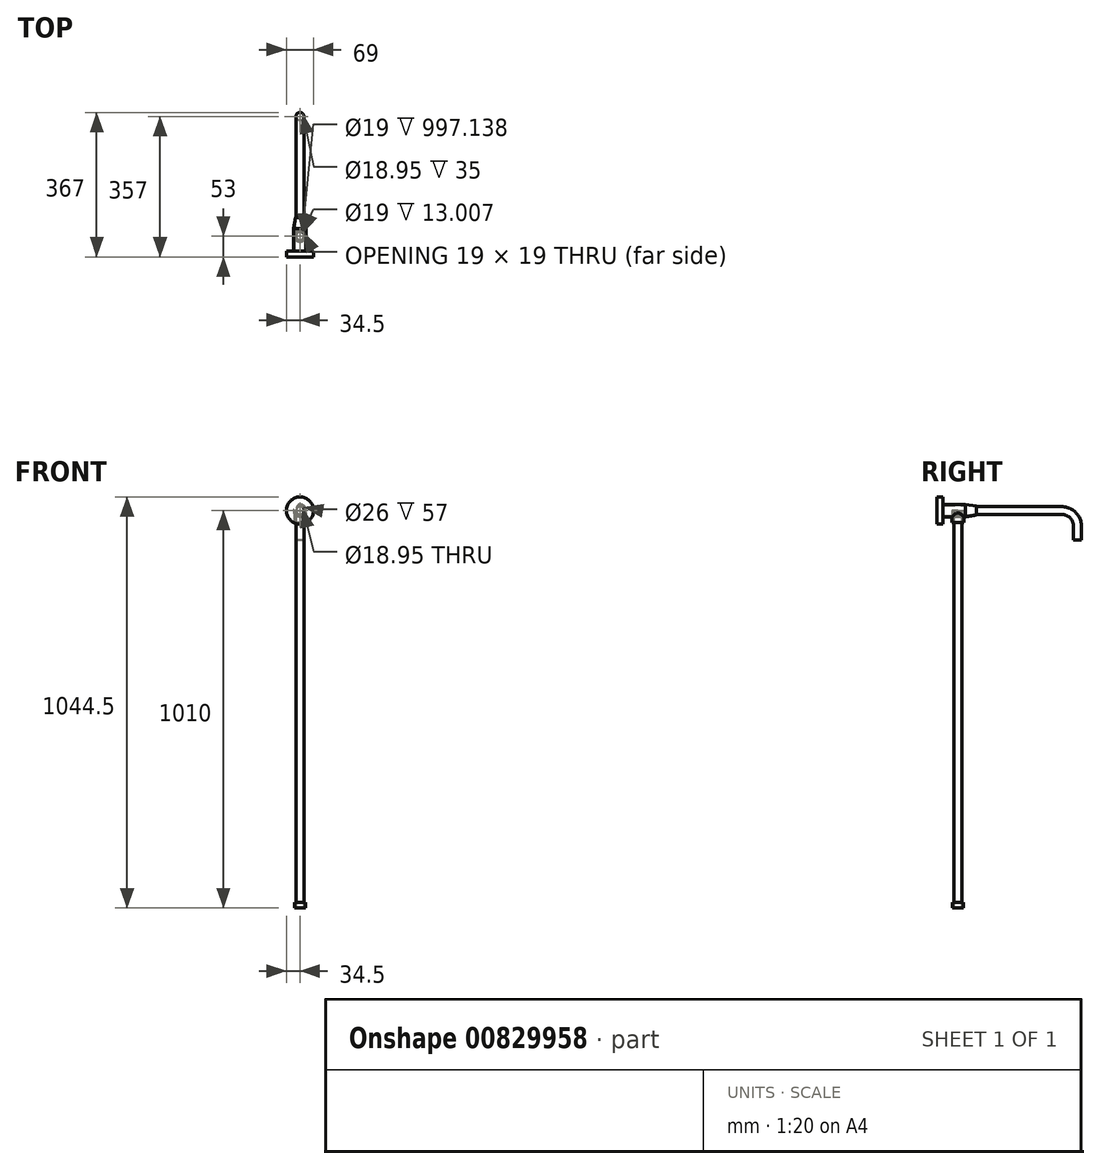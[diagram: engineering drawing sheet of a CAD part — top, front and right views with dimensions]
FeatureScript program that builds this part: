
annotation { "Feature Type Name" : "Feature", "Feature Type Description" : "" }
export const myFeature = defineFeature(function(context is Context, id is Id, definition is map)
    precondition{}
    {
        {
            var Q0;
            Q0=qCreatedBy(makeId("Top.planeOp"),FACE);
            var sketch = newSketch(context, id + "F0", { "sketchPlane" : qUnion([Q0])});
            skCircle(sketch, "E0", {"center": v(0, 0) * mm, "radius": 10 * mm});
            skCircle(sketch, "E1", {"center": v(0, 0) * mm, "radius": 9.5 * mm});
            skSolve(sketch);
        }
        {
            var Q0;
            Q0=makeQuery(id+"F0.imprint","IMPRINT",FACE,{"disambiguationData":[TD([[makeQuery(id+"F0.imprint","IMPRINT",EDGE,{"derivedFrom":sQuery(id+"F0.wireOp",EDGE,"E0")}),1.0]])]});
            extrude(context, id + "F1", {"entities" : qUnion([Q0]), "depth" : 980 * mm});
        }
        {
            var Q0;
            Q0=qCreatedBy(makeId("Top.planeOp"),FACE);
            var sketch = newSketch(context, id + "F2", { "sketchPlane" : qUnion([Q0])});
            skCircle(sketch, "E2", {"center": v(0, 0) * mm, "radius": 14 * mm});
            skCircle(sketch, "E3.0", {"center": v(0, 0) * mm, "radius": 9.5 * mm});
            skSolve(sketch);
        }
        {
            var Q0;
            Q0=makeQuery(id+"F2.imprint","IMPRINT",FACE,{"disambiguationData":[TD([[makeQuery(id+"F2.imprint","IMPRINT",EDGE,{"derivedFrom":sQuery(id+"F2.wireOp",EDGE,"E2")}),1.0]])]});
            extrude(context, id + "F3", {"entities" : qUnion([Q0]), "operationType" : NewBodyOperationType.ADD, "depth" : 14 * mm});
        }
        {
            var Q0;
            Q0=makeQuery(id+"F1.opExtrude","CAP_FACE",FACE,{"disambiguationData":[OSD([sQuery(id+"F0.wireOp",EDGE,"E0"),sQuery(id+"F0.wireOp",EDGE,"E1")])],"isStart":false});
            var sketch = newSketch(context, id + "F4", { "sketchPlane" : qUnion([Q0])});
            skCircle(sketch, "E4", {"center": v(0, 0) * mm, "radius": 15 * mm});
            skCircle(sketch, "E5.0", {"center": v(0, 0) * mm, "radius": 9.5 * mm});
            skSolve(sketch);
        }
        {
            var Q0;
            Q0=qSketchRegion(id+"F4",true);
            extrude(context, id + "F5", {"entities" : qUnion([Q0]), "operationType" : NewBodyOperationType.ADD, "depth" : 30 * mm});
        }
        {
            var Q0;
            Q0=qCreatedBy(makeId("Front.planeOp"),FACE);
            var sketch = newSketch(context, id + "F6", { "sketchPlane" : qUnion([Q0])});
            skCircle(sketch, "E6", {"center": v(0, 1010) * mm, "radius": 16 * mm});
            skCircle(sketch, "E7", {"center": v(0, 1010) * mm, "radius": 13 * mm});
            skSolve(sketch);
        }
        {
            var Q0;
            Q0=makeQuery(id+"F6.imprint","IMPRINT",FACE,{"disambiguationData":[TD([[makeQuery(id+"F6.imprint","IMPRINT",EDGE,{"derivedFrom":sQuery(id+"F6.wireOp",EDGE,"E6")}),1.0]])]});
            extrude(context, id + "F7", {"entities" : qUnion([Q0]), "operationType" : NewBodyOperationType.ADD, "depth" : 53 * mm});
        }
        {
            var Q0;
            Q0=qSketchRegion(id+"F6",true);
            extrude(context, id + "F8", {"entities" : qUnion([Q0]), "operationType" : NewBodyOperationType.ADD, "oppositeDirection" : true, "depth" : 19 * mm});
        }
        {
            var Q0;
            Q0=makeQuery(id+"F7.opExtrude","CAP_FACE",FACE,{"disambiguationData":[OSD([sQuery(id+"F6.wireOp",EDGE,"E6"),sQuery(id+"F6.wireOp",EDGE,"E7")])],"isStart":false});
            var sketch = newSketch(context, id + "F9", { "sketchPlane" : qUnion([Q0])});
            skCircle(sketch, "E8", {"center": v(0, 1010) * mm, "radius": 34.5 * mm});
            skSolve(sketch);
        }
        {
            var Q0;
            Q0=qSketchRegion(id+"F9",true);
            extrude(context, id + "F10", {"entities" : qUnion([Q0]), "operationType" : NewBodyOperationType.ADD, "oppositeDirection" : true, "depth" : 15 * mm});
        }
        {
            var Q0;
            Q0=qCreatedBy(makeId("Right.planeOp"),FACE);
            var sketch = newSketch(context, id + "F11", { "sketchPlane" : qUnion([Q0])});
            skLineSegment(sketch, "E9", {"start": v(19, 1026) * mm, "end": v(47, 1021.5) * mm});
            skLineSegment(sketch, "E10.0", {"start": v(19, 994) * mm, "end": v(19, 1026) * mm, "construction": true});
            skLineSegment(sketch, "E11", {"start": v(19, 1010) * mm, "end": v(231.63, 1010) * mm, "construction": true});
            skLineSegment(sketch, "E12", {"start": v(19, 1023.97) * mm, "end": v(47, 1019.47) * mm});
            skLineSegment(sketch, "E13", {"start": v(47, 1021.5) * mm, "end": v(47, 1020) * mm});
            skLineSegment(sketch, "E14", {"start": v(19, 1023.97) * mm, "end": v(19, 1026) * mm});
            skLineSegment(sketch, "E15", {"start": v(47, 1020) * mm, "end": v(264, 1020) * mm});
            skLineSegment(sketch, "E16", {"start": v(47, 1019.47) * mm, "end": v(264, 1019.47) * mm});
            skLineSegment(sketch, "E17", {"start": v(264, 1019.47) * mm, "end": v(264, 1020) * mm});
            skSolve(sketch);
        }
        {
            var Q0;
            Q0=qSketchRegion(id+"F11",true);
            var Q1;
            Q1=sQuery(id+"F11.wireOp",EDGE,"E11");
            revolve(context, id + "F12", {"operationType" : NewBodyOperationType.ADD, "entities" : qUnion([Q0]), "axis" : qUnion([Q1]), "revolveType" : RevolveType.FULL});
        }
        {
            var Q0;
            Q0=qCreatedBy(makeId("Right.planeOp"),FACE);
            var sketch = newSketch(context, id + "F13", { "sketchPlane" : qUnion([Q0])});
            skLineSegment(sketch, "E18.0", {"start": v(264, 1000) * mm, "end": v(264, 1020) * mm, "construction": true});
            skArc(sketch, "E19", {"start": v(264, 1010) * mm, "mid": v(292.28, 998.28) * mm, "end": v(304, 970) * mm});
            skLineSegment(sketch, "E20", {"start": v(264, 970) * mm, "end": v(304, 970) * mm, "construction": true});
            skSolve(sketch);
        }
        {
            var Q0;
            Q0=makeQuery(id+"F12.opRevolve","SWEPT_FACE",FACE,{"disambiguationData":[OSD([sQuery(id+"F11.wireOp",EDGE,"E17")])]});
            var Q1;
            Q1=sQuery(id+"F13.wireOp",EDGE,"E19");
            sweep(context, id + "F14", {"operationType" : NewBodyOperationType.ADD, "profiles" : qUnion([Q0]), "path" : qUnion([Q1])});
        }
        {
            var Q0;
            Q0=makeQuery(id+"F14.opSweep","CAP_FACE",FACE,{"disambiguationData":[OSD([sQuery(id+"F11.wireOp",EDGE,"E17"),sQuery(id+"F13.wireOp",VERTEX,"E19.end")])],"isStart":false});
            extrude(context, id + "F15", {"entities" : qUnion([Q0]), "operationType" : NewBodyOperationType.ADD, "depth" : 35 * mm});
        }
    });
